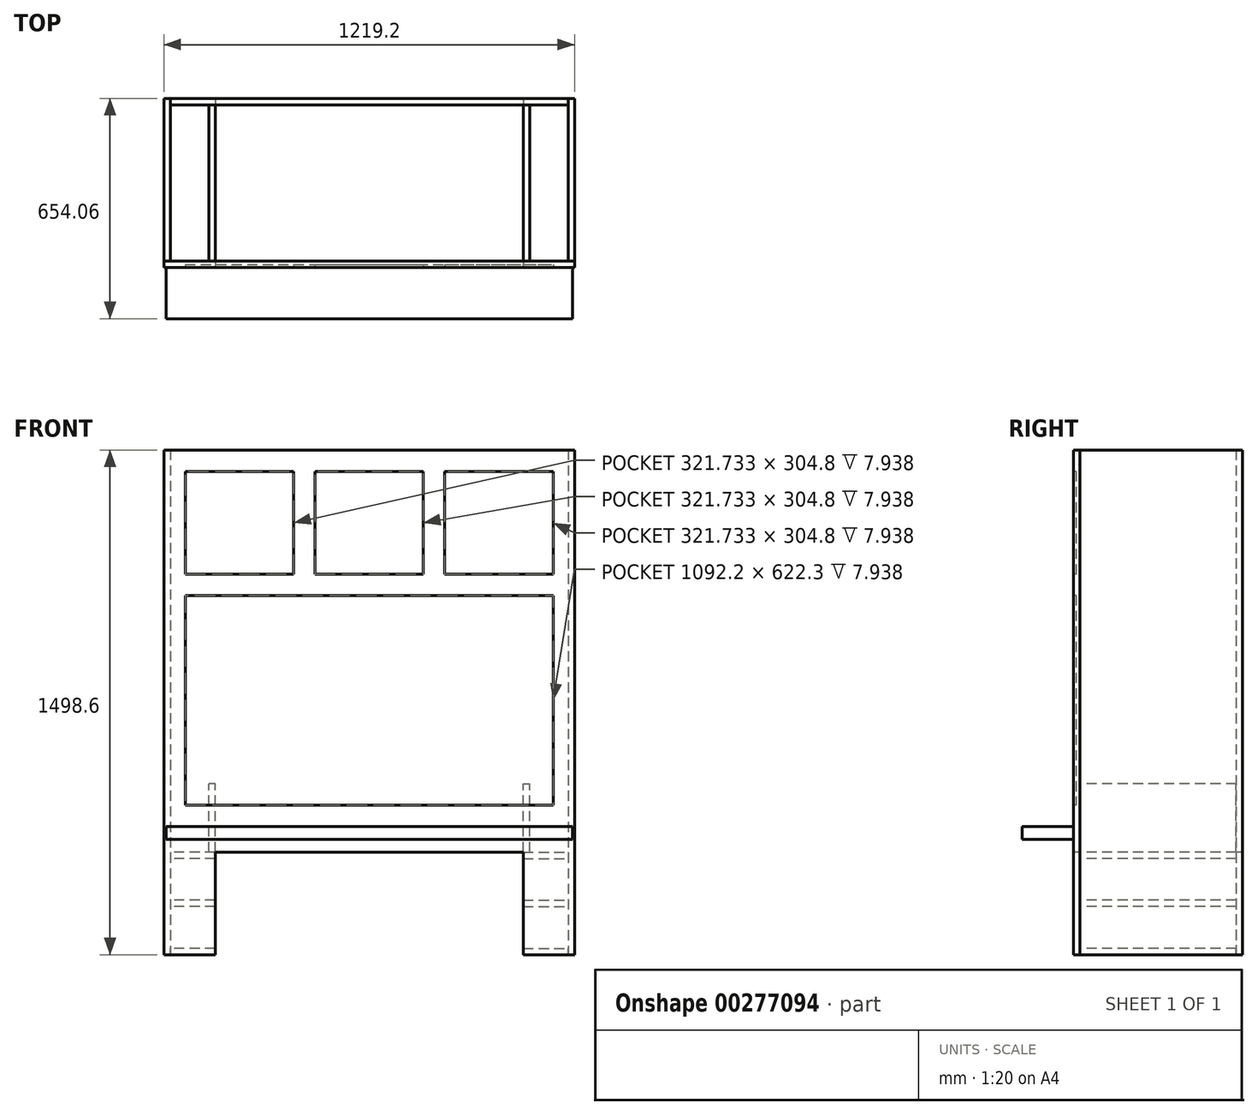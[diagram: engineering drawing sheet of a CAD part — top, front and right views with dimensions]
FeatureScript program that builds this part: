
annotation { "Feature Type Name" : "Feature", "Feature Type Description" : "" }
export const myFeature = defineFeature(function(context is Context, id is Id, definition is map)
    precondition{}
    {
        {
            var Q0;
            Q0=qCreatedBy(makeId("Top.planeOp"),FACE);
            var sketch = newSketch(context, id + "F0", { "sketchPlane" : qUnion([Q0])});
            skLineSegment(sketch, "E0.bottom", {"start": v(-609.6, 250.83) * mm, "end": v(609.6, 250.83) * mm, "construction": true});
            skLineSegment(sketch, "E0.top", {"start": v(-609.6, -250.83) * mm, "end": v(609.6, -250.83) * mm, "construction": true});
            skLineSegment(sketch, "E0.left", {"start": v(-609.6, 250.82) * mm, "end": v(-609.6, -250.83) * mm, "construction": true});
            skLineSegment(sketch, "E0.right", {"start": v(609.6, 250.82) * mm, "end": v(609.6, -250.82) * mm, "construction": true});
            skLineSegment(sketch, "E1", {"start": v(0, 250.83) * mm, "end": v(0, -250.83) * mm, "construction": true});
            skLineSegment(sketch, "E2", {"start": v(-609.6, 0) * mm, "end": v(609.6, 0) * mm, "construction": true});
            skSolve(sketch);
        }
        {
            var Q0;
            Q0=qCreatedBy(makeId("Front.planeOp"),FACE);
            var sketch = newSketch(context, id + "F1", { "sketchPlane" : qUnion([Q0])});
            skLineSegment(sketch, "E3", {"start": v(-609.6, 0) * mm, "end": v(-609.6, 1498.6) * mm, "construction": true});
            skSolve(sketch);
        }
        {
            var Q0;
            Q0=qCreatedBy(makeId("Top.planeOp"),FACE);
            var sketch = newSketch(context, id + "F2", { "sketchPlane" : qUnion([Q0])});
            skLineSegment(sketch, "E4.bottom", {"start": v(-609.6, -250.82) * mm, "end": v(609.6, -250.82) * mm});
            skLineSegment(sketch, "E4.top", {"start": v(-609.6, -231.77) * mm, "end": v(609.6, -231.77) * mm});
            skLineSegment(sketch, "E4.left", {"start": v(-609.6, -250.82) * mm, "end": v(-609.6, -231.77) * mm});
            skLineSegment(sketch, "E4.right", {"start": v(609.6, -250.82) * mm, "end": v(609.6, -231.77) * mm});
            skSolve(sketch);
        }
        {
            var Q0;
            Q0 = qSketchRegion(id + "F2", true);
            var Q1;
            Q1=sQuery(id+"F1.wireOp",VERTEX,"E3.end");
            extrude(context, id + "F3", {"entities" : qUnion([Q0]), "endBound" : BoundingType.UP_TO_VERTEX, "endBoundEntityVertex" : qUnion([Q1]), "depth" : 25.4 * mm});
        }
        {
            var Q0;
            Q0=qCreatedBy(makeId("Top.planeOp"),FACE);
            var sketch = newSketch(context, id + "F4", { "sketchPlane" : qUnion([Q0])});
            skLineSegment(sketch, "E5.bottom", {"start": v(-609.6, 250.82) * mm, "end": v(-590.55, 250.82) * mm});
            skLineSegment(sketch, "E5.top", {"start": v(-609.6, -231.77) * mm, "end": v(-590.55, -231.77) * mm});
            skLineSegment(sketch, "E5.left", {"start": v(-609.6, 250.82) * mm, "end": v(-609.6, -231.77) * mm});
            skLineSegment(sketch, "E5.right", {"start": v(-590.55, 250.82) * mm, "end": v(-590.55, -231.77) * mm});
            skLineSegment(sketch, "E6.MirrorCS", {"start": v(609.6, -231.77) * mm, "end": v(590.55, -231.77) * mm});
            skLineSegment(sketch, "E7.MirrorCS", {"start": v(609.6, 250.82) * mm, "end": v(590.55, 250.82) * mm});
            skLineSegment(sketch, "E8.MirrorCS", {"start": v(609.6, 250.82) * mm, "end": v(609.6, -231.77) * mm});
            skLineSegment(sketch, "E9.MirrorCS", {"start": v(590.55, 250.82) * mm, "end": v(590.55, -231.77) * mm});
            skSolve(sketch);
        }
        {
            var Q0;
            Q0 = qSketchRegion(id + "F4", true);
            var Q1;
            Q1=makeQuery(id+"F3.opExtrude","CAP_FACE",FACE,{"disambiguationData":[OSD([sQuery(id+"F2.wireOp",EDGE,"E4.bottom"),sQuery(id+"F2.wireOp",EDGE,"E4.top"),sQuery(id+"F2.wireOp",EDGE,"E4.left"),sQuery(id+"F2.wireOp",EDGE,"E4.right")])],"isStart":false});
            extrude(context, id + "F5", {"entities" : qUnion([Q0]), "endBound" : BoundingType.UP_TO_SURFACE, "endBoundEntityFace" : qUnion([Q1]), "depth" : 25.4 * mm});
        }
        {
            var Q0;
            Q0=makeQuery(id+"F5.opExtrude","SWEPT_FACE",FACE,{"disambiguationData":[OSD([sQuery(id+"F4.wireOp",EDGE,"E5.bottom")])]});
            var sketch = newSketch(context, id + "F6", { "sketchPlane" : qUnion([Q0])});
            skLineSegment(sketch, "E10.bottom", {"start": v(590.55, 1498.6) * mm, "end": v(-590.55, 1498.6) * mm});
            skLineSegment(sketch, "E10.top", {"start": v(590.55, 0) * mm, "end": v(-590.55, 0) * mm});
            skLineSegment(sketch, "E10.left", {"start": v(590.55, 1498.6) * mm, "end": v(590.55, 0) * mm});
            skLineSegment(sketch, "E10.right", {"start": v(-590.55, 1498.6) * mm, "end": v(-590.55, 0) * mm});
            skSolve(sketch);
        }
        {
            var Q0;
            Q0 = qSketchRegion(id + "F6", true);
            extrude(context, id + "F7", {"entities" : qUnion([Q0]), "oppositeDirection" : true, "depth" : 19.05 * mm});
        }
        {
            var Q0;
            Q0=makeQuery(id+"F3.opExtrude","SWEPT_FACE",FACE,{"disambiguationData":[OSD([sQuery(id+"F2.wireOp",EDGE,"E4.bottom")])]});
            var sketch = newSketch(context, id + "F8", { "sketchPlane" : qUnion([Q0])});
            skLineSegment(sketch, "E11.bottom", {"start": v(-457.2, 0) * mm, "end": v(457.2, 0) * mm});
            skLineSegment(sketch, "E11.top", {"start": v(-457.2, 304.8) * mm, "end": v(457.2, 304.8) * mm});
            skLineSegment(sketch, "E11.left", {"start": v(-457.2, 0) * mm, "end": v(-457.2, 304.8) * mm});
            skLineSegment(sketch, "E11.right", {"start": v(457.2, 0) * mm, "end": v(457.2, 304.8) * mm});
            skLineSegment(sketch, "E12", {"start": v(-457.2, 304.8) * mm, "end": v(-609.6, 304.8) * mm, "construction": true});
            skLineSegment(sketch, "E13", {"start": v(457.2, 304.8) * mm, "end": v(609.6, 304.8) * mm, "construction": true});
            skSolve(sketch);
        }
        {
            var Q0;
            Q0 = qSketchRegion(id + "F8", true);
            var Q1;
            Q1=makeQuery(id+"F7.opExtrude","CAP_FACE",FACE,{"disambiguationData":[OSD([sQuery(id+"F6.wireOp",EDGE,"E10.bottom"),sQuery(id+"F6.wireOp",EDGE,"E10.top"),sQuery(id+"F6.wireOp",EDGE,"E10.left"),sQuery(id+"F6.wireOp",EDGE,"E10.right")])],"isStart":true});
            extrude(context, id + "F9", {"entities" : qUnion([Q0]), "operationType" : NewBodyOperationType.REMOVE, "endBound" : BoundingType.UP_TO_SURFACE, "oppositeDirection" : true, "endBoundEntityFace" : qUnion([Q1]), "depth" : 25.4 * mm});
        }
        {
            var Q0;
            Q0=makeQuery(id+"F3.opExtrude","SWEPT_FACE",FACE,{"disambiguationData":[OSD([sQuery(id+"F2.wireOp",EDGE,"E4.top")])]});
            var sketch = newSketch(context, id + "F10", { "sketchPlane" : qUnion([Q0])});
            skLineSegment(sketch, "E14.bottom", {"start": v(457.2, 0) * mm, "end": v(590.55, 0) * mm});
            skLineSegment(sketch, "E14.top", {"start": v(457.2, 19.05) * mm, "end": v(590.55, 19.05) * mm});
            skLineSegment(sketch, "E14.left", {"start": v(457.2, 0) * mm, "end": v(457.2, 19.05) * mm});
            skLineSegment(sketch, "E14.right", {"start": v(590.55, 0) * mm, "end": v(590.55, 19.05) * mm});
            skLineSegment(sketch, "E15.bottom", {"start": v(457.2, 304.8) * mm, "end": v(590.55, 304.8) * mm});
            skLineSegment(sketch, "E15.top", {"start": v(457.2, 285.75) * mm, "end": v(590.55, 285.75) * mm});
            skLineSegment(sketch, "E15.left", {"start": v(457.2, 304.8) * mm, "end": v(457.2, 285.75) * mm});
            skLineSegment(sketch, "E15.right", {"start": v(590.55, 304.8) * mm, "end": v(590.55, 285.75) * mm});
            skLineSegment(sketch, "E16.bottom", {"start": v(457.2, 161.93) * mm, "end": v(590.55, 161.93) * mm});
            skLineSegment(sketch, "E16.top", {"start": v(457.2, 142.88) * mm, "end": v(590.55, 142.88) * mm});
            skLineSegment(sketch, "E16.left", {"start": v(457.2, 161.93) * mm, "end": v(457.2, 142.88) * mm});
            skLineSegment(sketch, "E16.right", {"start": v(590.55, 161.93) * mm, "end": v(590.55, 142.88) * mm});
            skLineSegment(sketch, "E17", {"start": v(523.88, 285.75) * mm, "end": v(523.88, 161.93) * mm, "construction": true});
            skLineSegment(sketch, "E18", {"start": v(523.88, 142.88) * mm, "end": v(523.88, 19.05) * mm, "construction": true});
            skSolve(sketch);
        }
        {
            var Q0;
            Q0 = qSketchRegion(id + "F10", true);
            var Q1;
            Q1=makeQuery(id+"F7.opExtrude","CAP_FACE",FACE,{"disambiguationData":[OSD([sQuery(id+"F6.wireOp",EDGE,"E10.bottom"),sQuery(id+"F6.wireOp",EDGE,"E10.top"),sQuery(id+"F6.wireOp",EDGE,"E10.left"),sQuery(id+"F6.wireOp",EDGE,"E10.right")])],"isStart":false});
            extrude(context, id + "F11", {"entities" : qUnion([Q0]), "endBound" : BoundingType.UP_TO_SURFACE, "endBoundEntityFace" : qUnion([Q1]), "depth" : 25.4 * mm});
        }
        {
            var Q0;
            Q0=makeQuery(id+"F3.opExtrude","SWEPT_FACE",FACE,{"disambiguationData":[OSD([sQuery(id+"F2.wireOp",EDGE,"E4.top")])]});
            var sketch = newSketch(context, id + "F12", { "sketchPlane" : qUnion([Q0])});
            skLineSegment(sketch, "E19.bottom", {"start": v(457.2, 304.8) * mm, "end": v(476.25, 304.8) * mm});
            skLineSegment(sketch, "E19.top", {"start": v(457.2, 508) * mm, "end": v(476.25, 508) * mm});
            skLineSegment(sketch, "E19.left", {"start": v(457.2, 304.8) * mm, "end": v(457.2, 508) * mm});
            skLineSegment(sketch, "E19.right", {"start": v(476.25, 304.8) * mm, "end": v(476.25, 508) * mm});
            skSolve(sketch);
        }
        {
            var Q0;
            Q0 = qSketchRegion(id + "F12", true);
            var Q1;
            Q1=makeQuery(id+"F7.opExtrude","CAP_FACE",FACE,{"disambiguationData":[OSD([sQuery(id+"F6.wireOp",EDGE,"E10.bottom"),sQuery(id+"F6.wireOp",EDGE,"E10.top"),sQuery(id+"F6.wireOp",EDGE,"E10.left"),sQuery(id+"F6.wireOp",EDGE,"E10.right")])],"isStart":false});
            extrude(context, id + "F13", {"entities" : qUnion([Q0]), "endBound" : BoundingType.UP_TO_SURFACE, "endBoundEntityFace" : qUnion([Q1]), "depth" : 25.4 * mm});
        }
        {
            var Q0;
            Q0=makeQuery(id+"F13.opExtrude","SWEPT_BODY",BODY,{"disambiguationData":[OSD([sQuery(id+"F12.wireOp",EDGE,"E19.bottom"),sQuery(id+"F12.wireOp",EDGE,"E19.top"),sQuery(id+"F12.wireOp",EDGE,"E19.left"),sQuery(id+"F12.wireOp",EDGE,"E19.right")])]});
            var Q1;
            Q1=makeQuery(id+"F11.opExtrude","SWEPT_BODY",BODY,{"disambiguationData":[OSD([sQuery(id+"F10.wireOp",EDGE,"E16.bottom"),sQuery(id+"F10.wireOp",EDGE,"E16.top"),sQuery(id+"F10.wireOp",EDGE,"E16.left"),sQuery(id+"F10.wireOp",EDGE,"E16.right")])]});
            var Q2;
            Q2=makeQuery(id+"F11.opExtrude","SWEPT_BODY",BODY,{"disambiguationData":[OSD([sQuery(id+"F10.wireOp",EDGE,"E15.bottom"),sQuery(id+"F10.wireOp",EDGE,"E15.top"),sQuery(id+"F10.wireOp",EDGE,"E15.left"),sQuery(id+"F10.wireOp",EDGE,"E15.right")])]});
            var Q3;
            Q3=makeQuery(id+"F11.opExtrude","SWEPT_BODY",BODY,{"disambiguationData":[OSD([sQuery(id+"F10.wireOp",EDGE,"E14.bottom"),sQuery(id+"F10.wireOp",EDGE,"E14.top"),sQuery(id+"F10.wireOp",EDGE,"E14.left"),sQuery(id+"F10.wireOp",EDGE,"E14.right")])]});
            var Q4;
            Q4=qCreatedBy(makeId("Right.planeOp"),FACE);
            mirror(context, id + "F14", {"entities" : qUnion([Q0, Q1, Q2, Q3]), "mirrorPlane" : qUnion([Q4])});
        }
        {
            var Q0;
            Q0=makeQuery(id+"F3.opExtrude","SWEPT_FACE",FACE,{"disambiguationData":[OSD([sQuery(id+"F2.wireOp",EDGE,"E4.bottom")])]});
            var sketch = newSketch(context, id + "F15", { "sketchPlane" : qUnion([Q0])});
            skLineSegment(sketch, "E20.bottom", {"start": v(-603.25, 381) * mm, "end": v(603.25, 381) * mm});
            skLineSegment(sketch, "E20.top", {"start": v(-603.25, 342.9) * mm, "end": v(603.25, 342.9) * mm});
            skLineSegment(sketch, "E20.left", {"start": v(-603.25, 381) * mm, "end": v(-603.25, 342.9) * mm});
            skLineSegment(sketch, "E20.right", {"start": v(603.25, 381) * mm, "end": v(603.25, 342.9) * mm});
            skSolve(sketch);
        }
        {
            var Q0;
            Q0 = qSketchRegion(id + "F15", true);
            extrude(context, id + "F16", {"entities" : qUnion([Q0]), "depth" : 152.4 * mm});
        }
        {
            var Q0;
            Q0=makeQuery(id+"F3.opExtrude","SWEPT_FACE",FACE,{"disambiguationData":[OSD([sQuery(id+"F2.wireOp",EDGE,"E4.bottom")])]});
            var sketch = newSketch(context, id + "F17", { "sketchPlane" : qUnion([Q0])});
            skLineSegment(sketch, "E21.bottom", {"start": v(-546.1, 1435.1) * mm, "end": v(-224.37, 1435.1) * mm});
            skLineSegment(sketch, "E21.top", {"start": v(-546.1, 1130.3) * mm, "end": v(-224.37, 1130.3) * mm});
            skLineSegment(sketch, "E21.left", {"start": v(-546.1, 1435.1) * mm, "end": v(-546.1, 1130.3) * mm});
            skLineSegment(sketch, "E21.right", {"start": v(-224.37, 1435.1) * mm, "end": v(-224.37, 1130.3) * mm});
            skLineSegment(sketch, "E22.bottom", {"start": v(-160.87, 1435.1) * mm, "end": v(160.87, 1435.1) * mm});
            skLineSegment(sketch, "E22.top", {"start": v(-160.87, 1130.3) * mm, "end": v(160.87, 1130.3) * mm});
            skLineSegment(sketch, "E22.left", {"start": v(-160.87, 1435.1) * mm, "end": v(-160.87, 1130.3) * mm});
            skLineSegment(sketch, "E22.right", {"start": v(160.87, 1435.1) * mm, "end": v(160.87, 1130.3) * mm});
            skLineSegment(sketch, "E23.bottom", {"start": v(224.37, 1435.1) * mm, "end": v(546.1, 1435.1) * mm});
            skLineSegment(sketch, "E23.top", {"start": v(224.37, 1130.3) * mm, "end": v(546.1, 1130.3) * mm});
            skLineSegment(sketch, "E23.left", {"start": v(224.37, 1435.1) * mm, "end": v(224.37, 1130.3) * mm});
            skLineSegment(sketch, "E23.right", {"start": v(546.1, 1435.1) * mm, "end": v(546.1, 1130.3) * mm});
            skLineSegment(sketch, "E24.bottom", {"start": v(-546.1, 1066.8) * mm, "end": v(546.1, 1066.8) * mm});
            skLineSegment(sketch, "E24.top", {"start": v(-546.1, 444.5) * mm, "end": v(546.1, 444.5) * mm});
            skLineSegment(sketch, "E24.left", {"start": v(-546.1, 1066.8) * mm, "end": v(-546.1, 444.5) * mm});
            skLineSegment(sketch, "E24.right", {"start": v(546.1, 1066.8) * mm, "end": v(546.1, 444.5) * mm});
            skSolve(sketch);
        }
        {
            var Q0;
            Q0 = qSketchRegion(id + "F17", true);
            extrude(context, id + "F18", {"entities" : qUnion([Q0]), "operationType" : NewBodyOperationType.REMOVE, "oppositeDirection" : true, "depth" : 7.94 * mm});
        }
    });
